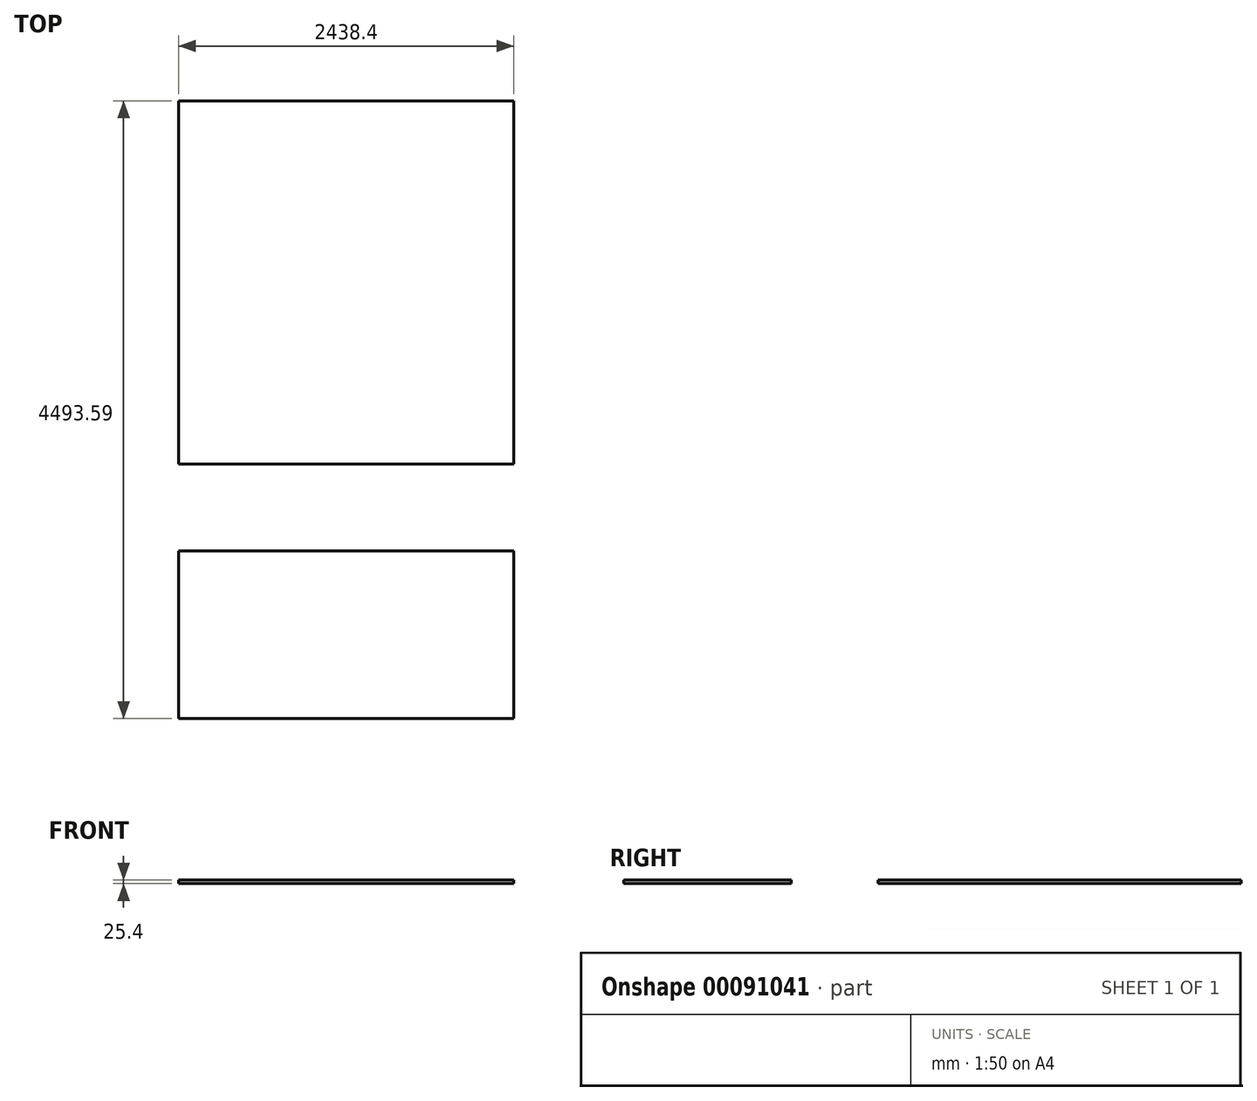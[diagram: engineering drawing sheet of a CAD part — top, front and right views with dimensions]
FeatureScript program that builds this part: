
annotation { "Feature Type Name" : "Feature", "Feature Type Description" : "" }
export const myFeature = defineFeature(function(context is Context, id is Id, definition is map)
    precondition{}
    {
        {
            var Q0;
            Q0=qCreatedBy(makeId("Top.planeOp"),FACE);
            var sketch = newSketch(context, id + "F0", { "sketchPlane" : qUnion([Q0])});
            skLineSegment(sketch, "E0.bottom", {"start": v(-1220.61, 1211.55) * mm, "end": v(1217.79, 1211.55) * mm});
            skLineSegment(sketch, "E0.top", {"start": v(-1220.61, -1430.05) * mm, "end": v(1217.79, -1430.05) * mm});
            skLineSegment(sketch, "E0.left", {"start": v(-1220.61, 1211.55) * mm, "end": v(-1220.61, -1430.05) * mm});
            skLineSegment(sketch, "E0.right", {"start": v(1217.79, 1211.55) * mm, "end": v(1217.79, -1430.05) * mm});
            skLineSegment(sketch, "E1", {"start": v(-1220.61, -2062.84) * mm, "end": v(1217.79, -2062.84) * mm});
            skLineSegment(sketch, "E2", {"start": v(1217.79, -2062.84) * mm, "end": v(1217.79, -3282.04) * mm});
            skLineSegment(sketch, "E3", {"start": v(1217.79, -3282.04) * mm, "end": v(-1220.61, -3282.04) * mm});
            skLineSegment(sketch, "E4", {"start": v(-1220.61, -3282.04) * mm, "end": v(-1220.61, -2062.84) * mm});
            skSolve(sketch);
        }
        {
            var Q0;
            Q0=makeQuery(id+"F0.imprint","IMPRINT",FACE,{"disambiguationData":[TD([[makeQuery(id+"F0.imprint","IMPRINT",EDGE,{"derivedFrom":sQuery(id+"F0.wireOp",EDGE,"E0.bottom")}),-1.0]])]});
            extrude(context, id + "F1", {"entities" : qUnion([Q0]), "depth" : 25.4 * mm});
        }
        {
            var Q0;
            Q0=makeQuery(id+"F0.imprint","IMPRINT",FACE,{"disambiguationData":[TD([[makeQuery(id+"F0.imprint","IMPRINT",EDGE,{"derivedFrom":sQuery(id+"F0.wireOp",EDGE,"E1")}),-1.0]])]});
            extrude(context, id + "F2", {"entities" : qUnion([Q0]), "depth" : 25.4 * mm});
        }
    });
